# Revit family: CL
name_source: partatom
category: Lighting Fixtures
units: mm (PartAtom-declared; Revit-internal decimal feet)

## family parameters
Cut with Voids When Loaded = No
Host = Face
Light Source = No
OmniClass Number = 23.80.70.11.21
OmniClass Title = Emergency Lighting
Part Type = Normal
Room Calculation Point = No
Round Connector Dimension = Use Diameter
Shared = No

## types (1)
- CL
    Apparent Load = 50 VA
    Connector Description = Lighting Connector
    Default Elevation = 48 "
    Description = The CL series is a recessed, self-contained emergency light
with fully automatic operation suitable for wall or ceiling mount
applications.
    Finish = Finish -  White
    Glass = Glass
    Lamp = Halogen lamp
    Load Classification = Lighting
    Manufacturer = Dual-Lite
    Model = CL
    Product Material = Finish -  Steel
    URL = https://www.currentlighting.com
    Voltage = 120 V
    Wattage Comments = 12-75 Watt

## geometry (parser evidence)
native form markers: Blend x2, Sweep x8
no freeform markers — native parametric forms only
